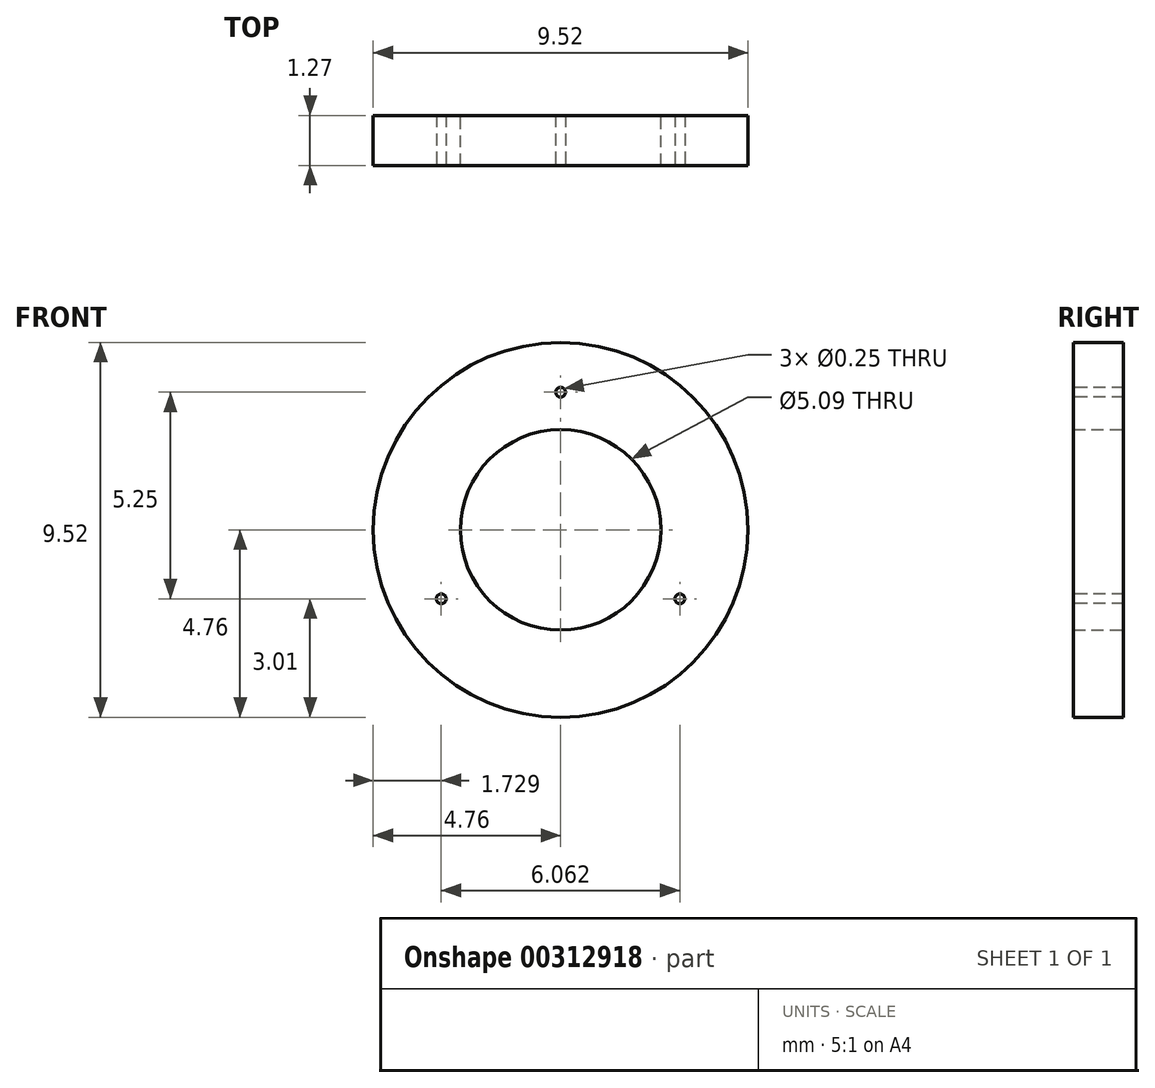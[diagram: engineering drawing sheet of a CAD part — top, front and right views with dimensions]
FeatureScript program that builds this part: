
annotation { "Feature Type Name" : "Feature", "Feature Type Description" : "" }
export const myFeature = defineFeature(function(context is Context, id is Id, definition is map)
    precondition{}
    {
        {
            var Q0;
            Q0=qCreatedBy(makeId("Front.planeOp"),FACE);
            var sketch = newSketch(context, id + "F0", { "sketchPlane" : qUnion([Q0])});
            skCircle(sketch, "E0", {"center": v(0, 0) * mm, "radius": 4.76 * mm});
            skSolve(sketch);
        }
        {
            var Q0;
            Q0=makeQuery(id+"F0.imprint","IMPRINT",FACE,{"disambiguationData":[TD([[makeQuery(id+"F0.imprint","IMPRINT",EDGE,{"derivedFrom":sQuery(id+"F0.wireOp",EDGE,"E0")}),1.0]])]});
            var sketch = newSketch(context, id + "F1", { "sketchPlane" : qUnion([Q0])});
            skCircle(sketch, "E1", {"center": v(0, 0) * mm, "radius": 2.55 * mm});
            skSolve(sketch);
        }
        {
            var Q0;
            Q0=makeQuery(id+"F0.imprint","IMPRINT",FACE,{"disambiguationData":[TD([[makeQuery(id+"F0.imprint","IMPRINT",EDGE,{"derivedFrom":sQuery(id+"F0.wireOp",EDGE,"E0")}),1.0]])]});
            extrude(context, id + "F2", {"entities" : qUnion([Q0]), "depth" : 1.27 * mm});
        }
        {
            var Q0;
            Q0=makeQuery(id+"F1.imprint","IMPRINT",FACE,{"disambiguationData":[TD([[makeQuery(id+"F1.imprint","IMPRINT",EDGE,{"derivedFrom":sQuery(id+"F1.wireOp",EDGE,"E1")}),1.0]])]});
            extrude(context, id + "F3", {"entities" : qUnion([Q0]), "operationType" : NewBodyOperationType.REMOVE, "depth" : 12.7 * mm});
        }
        {
            var Q0;
            Q0=makeQuery(id+"F2.opExtrude","CAP_FACE",FACE,{"disambiguationData":[OSD([sQuery(id+"F0.wireOp",EDGE,"E0")])],"isStart":false});
            var sketch = newSketch(context, id + "F4", { "sketchPlane" : qUnion([Q0])});
            skCircle(sketch, "E2", {"center": v(0, 3.5) * mm, "radius": 0.12 * mm});
            skCircle(sketch, "E3.1.0", {"center": v(-3.03, -1.75) * mm, "radius": 0.12 * mm});
            skCircle(sketch, "E3.2.0", {"center": v(3.03, -1.75) * mm, "radius": 0.12 * mm});
            skPoint(sketch, "E3.center", {"position": v(0, 0) * mm});
            skSolve(sketch);
        }
        {
            var Q0;
            Q0=makeQuery(id+"F4.imprint","IMPRINT",FACE,{"disambiguationData":[TD([[makeQuery(id+"F4.imprint","IMPRINT",EDGE,{"derivedFrom":sQuery(id+"F4.wireOp",EDGE,"E2")}),1.0]])]});
            var Q1;
            Q1=makeQuery(id+"F4.imprint","IMPRINT",FACE,{"disambiguationData":[TD([[makeQuery(id+"F4.imprint","IMPRINT",EDGE,{"derivedFrom":sQuery(id+"F4.wireOp",EDGE,"E3.1.0")}),1.0]])]});
            var Q2;
            Q2=makeQuery(id+"F4.imprint","IMPRINT",FACE,{"disambiguationData":[TD([[makeQuery(id+"F4.imprint","IMPRINT",EDGE,{"derivedFrom":sQuery(id+"F4.wireOp",EDGE,"E3.2.0")}),1.0]])]});
            extrude(context, id + "F5", {"entities" : qUnion([Q0, Q1, Q2]), "operationType" : NewBodyOperationType.REMOVE, "oppositeDirection" : true, "depth" : 25.4 * mm});
        }
    });
